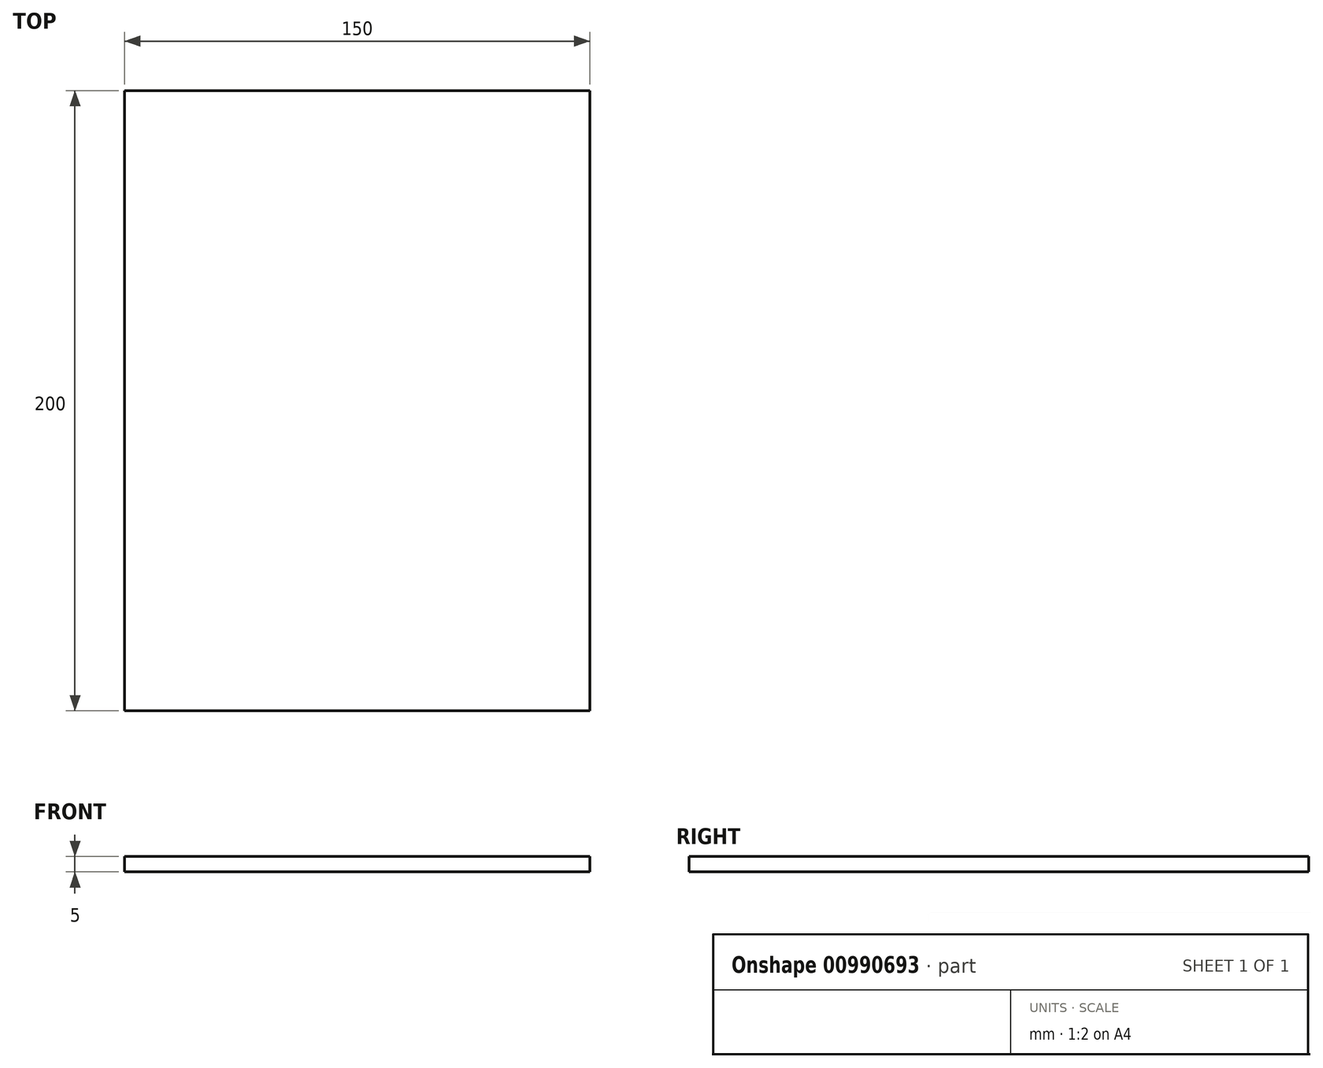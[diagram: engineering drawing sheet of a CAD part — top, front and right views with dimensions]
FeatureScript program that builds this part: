
annotation { "Feature Type Name" : "Feature", "Feature Type Description" : "" }
export const myFeature = defineFeature(function(context is Context, id is Id, definition is map)
    precondition{}
    {
        {
            assignVariable(context, id + "F0", {"name" : "MirrorThickness", "anyValue" : 5});
        }
        {
            var Q0;
            Q0=qCreatedBy(makeId("Top.planeOp"),FACE);
            var sketch = newSketch(context, id + "F1", { "sketchPlane" : qUnion([Q0])});
            skLineSegment(sketch, "E0.bottom", {"start": v(75, -100) * mm, "end": v(-75, -100) * mm});
            skLineSegment(sketch, "E0.top", {"start": v(75, 100) * mm, "end": v(-75, 100) * mm});
            skLineSegment(sketch, "E0.left", {"start": v(75, -100) * mm, "end": v(75, 100) * mm});
            skLineSegment(sketch, "E0.right", {"start": v(-75, -100) * mm, "end": v(-75, 100) * mm});
            skPoint(sketch, "E0.middle", {"position": v(0, 0) * mm});
            skSolve(sketch);
        }
        {
            var Q0;
            Q0=makeQuery(id+"F1.imprint","IMPRINT",FACE,{"disambiguationData":[TD([[makeQuery(id+"F1.imprint","IMPRINT",EDGE,{"derivedFrom":sQuery(id+"F1.wireOp",EDGE,"E0.bottom")}),-1.0]])]});
            extrude(context, id + "F2", {"entities" : qUnion([Q0]), "depth" : (getVariable(context, 'MirrorThickness')) * mm, "offsetDistance" : 25 * mm});
        }
    });
